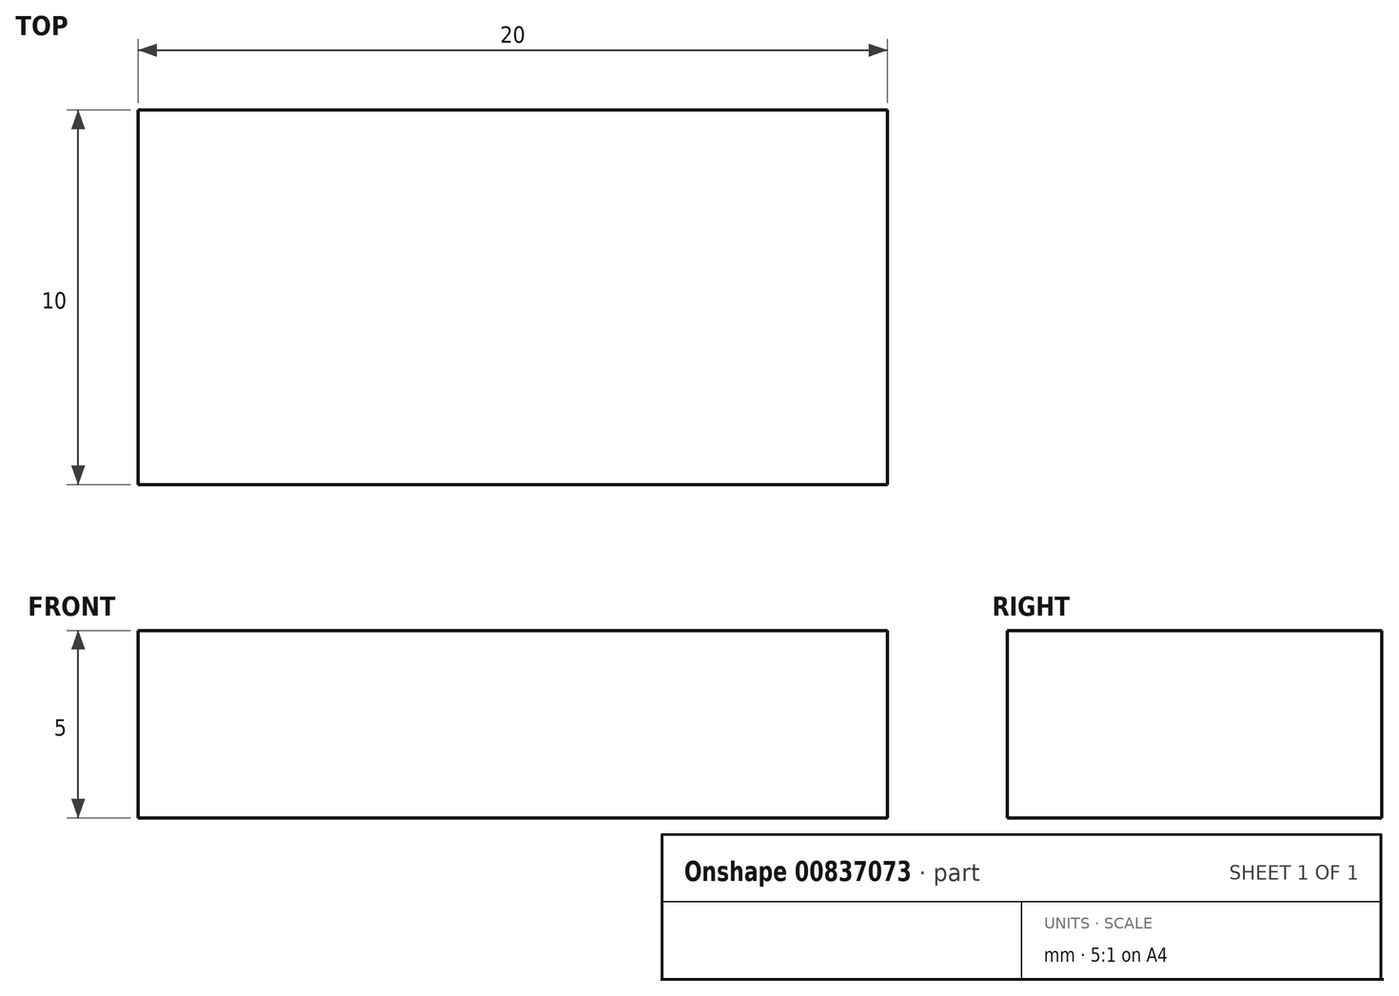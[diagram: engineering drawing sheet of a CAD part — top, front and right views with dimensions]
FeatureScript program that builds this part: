
annotation { "Feature Type Name" : "Feature", "Feature Type Description" : "" }
export const myFeature = defineFeature(function(context is Context, id is Id, definition is map)
    precondition{}
    {
        {
            var Q0;
            Q0=qCreatedBy(makeId("Top.planeOp"),FACE);
            var sketch = newSketch(context, id + "F0", { "sketchPlane" : qUnion([Q0])});
            skLineSegment(sketch, "E0.bottom", {"start": v(-12.43, 8.6) * mm, "end": v(7.57, 8.6) * mm});
            skLineSegment(sketch, "E0.top", {"start": v(-12.43, -1.4) * mm, "end": v(7.57, -1.4) * mm});
            skLineSegment(sketch, "E0.left", {"start": v(-12.43, 8.6) * mm, "end": v(-12.43, -1.4) * mm});
            skLineSegment(sketch, "E0.right", {"start": v(7.57, 8.6) * mm, "end": v(7.57, -1.4) * mm});
            skSolve(sketch);
        }
        {
            var Q0;
            Q0=makeQuery(id+"F0.imprint","IMPRINT",FACE,{"disambiguationData":[TD([[makeQuery(id+"F0.imprint","IMPRINT",EDGE,{"derivedFrom":sQuery(id+"F0.wireOp",EDGE,"E0.bottom")}),-1.0]])]});
            extrude(context, id + "F1", {"entities" : qUnion([Q0]), "depth" : 5 * mm, "offsetDistance" : 25 * mm});
        }
    });
